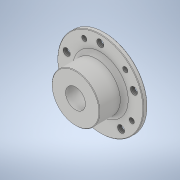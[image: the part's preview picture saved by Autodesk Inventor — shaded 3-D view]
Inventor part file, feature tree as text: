
AUTODESK INVENTOR PART (.ipt)
format: ipt  version: 2021 (Build 250183000, 183)  size: 223,744 bytes
history: native  units: in
note: dims shown in document units (in); Inventor stores cm internally (conversion verified against a paired STEP export)
features: thread x11, sketch x6, extrude x5, fillet x2, revolve x1, chamfer x1
ambient origin geometry x8: Origin, YZ Plane, XZ Plane, XY Plane, X Axis, Y Axis, Z Axis, Center Point
bodies: Solid1 (feature_tree)
feature tree (26):
  revolve  "Revolution1"  [1 undecoded]
  extrude  "Extrusion1"  Depth=0.26in
  extrude  "Extrusion2"  Depth=0.2in
  fillet  "Fillet1"  Radius=0.16in
  chamfer  "Chamfer1"  Distance=1.0in
  fillet  "Fillet2"  Radius=1.25in
  extrude  "Extrusion3"  Depth=0.26in TaperAngle=0.0deg
  thread  "Thread1"  [1 undecoded]
  thread  "Thread2"  [1 undecoded]
  thread  "Thread3"  [1 undecoded]
  thread  "Thread4"  [1 undecoded]
  thread  "Thread5"  [1 undecoded]
  thread  "Thread6"  [1 undecoded]
  extrude  "Extrusion4"  TaperAngle=45.0deg  [1 undecoded]
  extrude  "Extrusion5"  Depth=0.26in
  thread  "Thread7"  [1 undecoded]
  thread  "Thread8"  [1 undecoded]
  thread  "Thread9"  [1 undecoded]
  thread  "Thread10"  [1 undecoded]
  thread  "Thread11"  [1 undecoded]
  sketch  "Sketch1"  dims[d0=1.5in d1=1.56in]
  sketch  "Sketch2"  dims[d2=1.2in d3=0.26in]
  sketch  "Sketch3"  dims[d4=1.42in d5=0.2in d6=0.16in]
  sketch  "Sketch4"  dims[d7=0.52in]
  sketch  "Sketch5"  dims[d8=90.0deg]
  sketch  "Sketch6"  dims[d9=2.0in d10=1.0in d11=0.0in d12=1.25in d13=1.0in d14=0.0in d15=0.075in d16=0.03in d17=0.125in d18=45.0deg d19=0.25in d20=0.452in d21=0.48in d22=1.9685in d24=360.0deg d26=45.0deg d27=0.2in d28=0.2in d29=0.0in d30=0.435in d31=0.0in d32=0.435in d33=0.0in d34=0.435in d35=0.0in d36=0.435in d37=0.0in d38=0.435in d39=0.0in d40=0.435in d41=0.0in d42=1.0in d43=0.0in d44=0.325in d45=1.9685in d47=360.0deg d49=1.0in d50=0.0in d51=0.26in d52=0.0in d53=0.26in d54=0.0in d55=0.26in d56=0.0in d57=0.26in d58=0.0in d59=0.26in d60=0.0in]
note: 13 required parameter values undecoded (feature->parameter linkage not recoverable at this tier; creation-order binding heuristic only, values carry confidence <= 0.55)